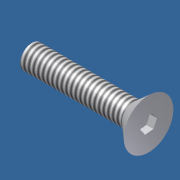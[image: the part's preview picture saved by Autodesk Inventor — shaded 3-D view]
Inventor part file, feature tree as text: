
AUTODESK INVENTOR PART (.ipt)
format: ipt  version: 2012 (Build 160160000, 160)  size: 95,744 bytes
history: native  units: in
note: dims shown in document units (in); Inventor stores cm internally (conversion verified against a paired STEP export)
features: sketch x2, revolve x1, thread x1, extrude x1
ambient origin geometry x8: Origin, YZ Plane, XZ Plane, XY Plane, X Axis, Y Axis, Z Axis, Center Point
bodies: Solid1 (feature_tree)
feature tree (5):
  revolve  "Revolution1"  [1 undecoded]
  thread  "Thread1"  [1 undecoded]
  extrude  "Extrusion1"  Depth=1.0in TaperAngle=0.0deg
  sketch  "Sketch1"  dims[d1=0.125in d2=0.161in d3=0.2655in]
  sketch  "Sketch2"  dims[d4=90.0deg d5=1.0in d6=0.0in d16=0.1562in d17=0.075in d18=0.0in d20=1.25in]
note: 2 required parameter values undecoded (feature->parameter linkage not recoverable at this tier; creation-order binding heuristic only, values carry confidence <= 0.55)